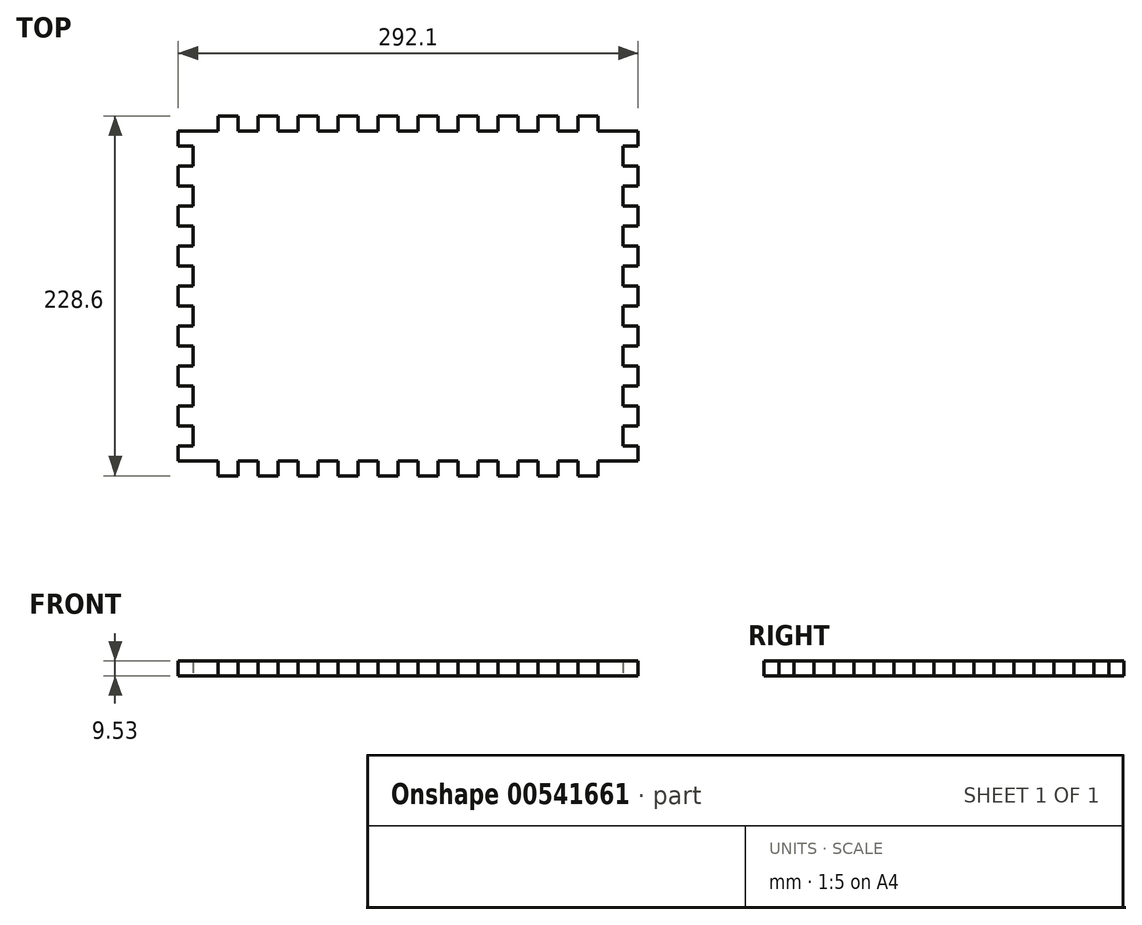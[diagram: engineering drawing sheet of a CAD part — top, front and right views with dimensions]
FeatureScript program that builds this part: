
annotation { "Feature Type Name" : "Feature", "Feature Type Description" : "" }
export const myFeature = defineFeature(function(context is Context, id is Id, definition is map)
    precondition{}
    {
        {
            var Q0;
            Q0=qCreatedBy(makeId("Top.planeOp"),FACE);
            var sketch = newSketch(context, id + "F0", { "sketchPlane" : qUnion([Q0])});
            skLineSegment(sketch, "E0.bottom", {"start": v(50.8, 0) * mm, "end": v(63.5, 0) * mm});
            skLineSegment(sketch, "E0.left", {"start": v(0, -9.53) * mm, "end": v(0, -19.05) * mm});
            skLineSegment(sketch, "E1", {"start": v(0, -9.53) * mm, "end": v(25.4, -9.53) * mm});
            skLineSegment(sketch, "E2", {"start": v(25.4, -9.53) * mm, "end": v(25.4, 0) * mm});
            skLineSegment(sketch, "E3", {"start": v(25.4, 0) * mm, "end": v(38.1, 0) * mm});
            skLineSegment(sketch, "E4", {"start": v(38.1, 0) * mm, "end": v(38.1, -9.53) * mm});
            skLineSegment(sketch, "E5", {"start": v(38.1, -9.53) * mm, "end": v(50.8, -9.53) * mm});
            skLineSegment(sketch, "E6", {"start": v(50.8, -9.53) * mm, "end": v(50.8, 0) * mm});
            skLineSegment(sketch, "E7", {"start": v(63.5, 0) * mm, "end": v(63.5, -9.52) * mm});
            skLineSegment(sketch, "E8", {"start": v(63.5, -9.52) * mm, "end": v(76.2, -9.52) * mm});
            skLineSegment(sketch, "E9", {"start": v(76.2, -9.52) * mm, "end": v(76.2, 0) * mm});
            skLineSegment(sketch, "E10", {"start": v(76.2, 0) * mm, "end": v(88.9, 0) * mm});
            skLineSegment(sketch, "E11", {"start": v(88.9, 0) * mm, "end": v(88.9, -9.52) * mm});
            skLineSegment(sketch, "E12", {"start": v(88.9, -9.52) * mm, "end": v(101.6, -9.52) * mm});
            skLineSegment(sketch, "E13", {"start": v(101.6, -9.52) * mm, "end": v(101.6, 0) * mm});
            skPoint(sketch, "E14.orphan", {"position": v(0, 0) * mm});
            skLineSegment(sketch, "E15.trimOffspring", {"start": v(101.6, 0) * mm, "end": v(114.3, 0) * mm});
            skLineSegment(sketch, "E16", {"start": v(114.3, 0) * mm, "end": v(114.3, -9.53) * mm});
            skLineSegment(sketch, "E17", {"start": v(114.3, -9.52) * mm, "end": v(127, -9.52) * mm});
            skLineSegment(sketch, "E18", {"start": v(127, -9.53) * mm, "end": v(127, 0) * mm});
            skLineSegment(sketch, "E19", {"start": v(127, 0) * mm, "end": v(139.7, 0) * mm});
            skLineSegment(sketch, "E20", {"start": v(139.7, 0) * mm, "end": v(139.7, -9.52) * mm});
            skLineSegment(sketch, "E21", {"start": v(139.7, -9.52) * mm, "end": v(152.4, -9.52) * mm});
            skLineSegment(sketch, "E22", {"start": v(152.4, -9.53) * mm, "end": v(152.4, 0) * mm});
            skLineSegment(sketch, "E23", {"start": v(152.4, 0) * mm, "end": v(165.1, 0) * mm});
            skLineSegment(sketch, "E24", {"start": v(165.1, 0) * mm, "end": v(165.1, -9.52) * mm});
            skLineSegment(sketch, "E25", {"start": v(165.1, -9.52) * mm, "end": v(177.8, -9.52) * mm});
            skLineSegment(sketch, "E26", {"start": v(177.8, -9.52) * mm, "end": v(177.8, 0) * mm});
            skLineSegment(sketch, "E27", {"start": v(177.8, 0) * mm, "end": v(190.5, 0) * mm});
            skLineSegment(sketch, "E28", {"start": v(190.5, 0) * mm, "end": v(190.5, -9.52) * mm});
            skLineSegment(sketch, "E29", {"start": v(190.5, -9.52) * mm, "end": v(203.2, -9.52) * mm});
            skLineSegment(sketch, "E30", {"start": v(203.2, -9.52) * mm, "end": v(203.2, 0) * mm});
            skLineSegment(sketch, "E31.trimOffspring", {"start": v(203.2, 0) * mm, "end": v(215.9, 0) * mm});
            skLineSegment(sketch, "E32", {"start": v(215.9, 0) * mm, "end": v(215.9, -9.52) * mm});
            skLineSegment(sketch, "E33", {"start": v(215.9, -9.52) * mm, "end": v(228.6, -9.52) * mm});
            skLineSegment(sketch, "E34", {"start": v(228.6, -9.52) * mm, "end": v(228.6, 0) * mm});
            skLineSegment(sketch, "E35.trimOffspring", {"start": v(228.6, 0) * mm, "end": v(241.3, 0) * mm});
            skLineSegment(sketch, "E36", {"start": v(241.3, 0) * mm, "end": v(241.3, -9.52) * mm});
            skLineSegment(sketch, "E37", {"start": v(241.3, -9.52) * mm, "end": v(254, -9.52) * mm});
            skLineSegment(sketch, "E38", {"start": v(254, -9.52) * mm, "end": v(254, 0) * mm});
            skLineSegment(sketch, "E39", {"start": v(254, 0) * mm, "end": v(266.7, 0) * mm});
            skLineSegment(sketch, "E40", {"start": v(266.7, 0) * mm, "end": v(266.7, -9.52) * mm});
            skLineSegment(sketch, "E41", {"start": v(266.7, -9.52) * mm, "end": v(292.1, -9.52) * mm});
            skPoint(sketch, "E42.orphan", {"position": v(292.1, 0) * mm});
            skLineSegment(sketch, "E43", {"start": v(0, -19.05) * mm, "end": v(9.52, -19.05) * mm});
            skLineSegment(sketch, "E44", {"start": v(9.52, -19.05) * mm, "end": v(9.52, -31.75) * mm});
            skLineSegment(sketch, "E45", {"start": v(9.52, -31.75) * mm, "end": v(0, -31.75) * mm});
            skLineSegment(sketch, "E46", {"start": v(0, -31.75) * mm, "end": v(0, -44.45) * mm});
            skLineSegment(sketch, "E47", {"start": v(0, -44.45) * mm, "end": v(9.52, -44.45) * mm});
            skLineSegment(sketch, "E48", {"start": v(9.52, -44.45) * mm, "end": v(9.52, -57.15) * mm});
            skLineSegment(sketch, "E49", {"start": v(9.52, -57.15) * mm, "end": v(0, -57.15) * mm});
            skLineSegment(sketch, "E50", {"start": v(0, -57.15) * mm, "end": v(0, -69.85) * mm});
            skLineSegment(sketch, "E51", {"start": v(0, -69.85) * mm, "end": v(9.52, -69.85) * mm});
            skLineSegment(sketch, "E52", {"start": v(9.52, -69.85) * mm, "end": v(9.52, -82.55) * mm});
            skLineSegment(sketch, "E53", {"start": v(9.52, -82.55) * mm, "end": v(0, -82.55) * mm});
            skLineSegment(sketch, "E54.trimOffspring", {"start": v(0, -82.55) * mm, "end": v(0, -95.25) * mm});
            skLineSegment(sketch, "E55", {"start": v(0, -95.25) * mm, "end": v(9.52, -95.25) * mm});
            skLineSegment(sketch, "E56", {"start": v(9.52, -95.25) * mm, "end": v(9.52, -107.95) * mm});
            skLineSegment(sketch, "E57", {"start": v(9.53, -107.95) * mm, "end": v(0, -107.95) * mm});
            skLineSegment(sketch, "E58", {"start": v(0, -107.95) * mm, "end": v(0, -120.65) * mm});
            skLineSegment(sketch, "E59", {"start": v(0, -120.65) * mm, "end": v(9.53, -120.65) * mm});
            skLineSegment(sketch, "E60", {"start": v(9.53, -120.65) * mm, "end": v(9.53, -133.35) * mm});
            skLineSegment(sketch, "E61", {"start": v(9.53, -133.35) * mm, "end": v(0, -133.35) * mm});
            skLineSegment(sketch, "E62", {"start": v(0, -133.35) * mm, "end": v(0, -146.05) * mm});
            skLineSegment(sketch, "E63", {"start": v(0, -146.05) * mm, "end": v(9.53, -146.05) * mm});
            skLineSegment(sketch, "E64", {"start": v(9.53, -146.05) * mm, "end": v(9.53, -158.75) * mm});
            skLineSegment(sketch, "E65", {"start": v(9.53, -158.75) * mm, "end": v(0, -158.75) * mm});
            skLineSegment(sketch, "E66.trimOffspring", {"start": v(0, -158.75) * mm, "end": v(0, -171.45) * mm});
            skLineSegment(sketch, "E67", {"start": v(0, -171.45) * mm, "end": v(9.53, -171.45) * mm});
            skLineSegment(sketch, "E68", {"start": v(9.53, -171.45) * mm, "end": v(9.53, -184.15) * mm});
            skLineSegment(sketch, "E69", {"start": v(9.53, -184.15) * mm, "end": v(0, -184.15) * mm});
            skLineSegment(sketch, "E70", {"start": v(0, -184.15) * mm, "end": v(0, -196.85) * mm});
            skLineSegment(sketch, "E71", {"start": v(0, -196.85) * mm, "end": v(9.53, -196.85) * mm});
            skLineSegment(sketch, "E72", {"start": v(9.53, -196.85) * mm, "end": v(9.53, -209.55) * mm});
            skLineSegment(sketch, "E73", {"start": v(9.53, -209.55) * mm, "end": v(0, -209.55) * mm});
            skLineSegment(sketch, "E74.trimOffspring", {"start": v(0, -209.55) * mm, "end": v(0, -219.07) * mm});
            skLineSegment(sketch, "E75", {"start": v(0, -219.07) * mm, "end": v(25.4, -219.07) * mm});
            skLineSegment(sketch, "E76", {"start": v(25.4, -219.08) * mm, "end": v(25.4, -228.6) * mm});
            skPoint(sketch, "E77.orphan", {"position": v(0, -228.6) * mm});
            skLineSegment(sketch, "E78", {"start": v(146.05, -9.52) * mm, "end": v(146.05, -60.11) * mm, "construction": true});
            skLineSegment(sketch, "E79", {"start": v(0, -114.3) * mm, "end": v(50, -114.3) * mm, "construction": true});
            skLineSegment(sketch, "E80.MirrorCS", {"start": v(292.1, -9.53) * mm, "end": v(292.1, -19.05) * mm});
            skLineSegment(sketch, "E81.MirrorCS", {"start": v(292.1, -19.05) * mm, "end": v(282.57, -19.05) * mm});
            skLineSegment(sketch, "E82.MirrorCS", {"start": v(282.57, -19.05) * mm, "end": v(282.57, -31.75) * mm});
            skLineSegment(sketch, "E83.MirrorCS", {"start": v(282.57, -31.75) * mm, "end": v(292.1, -31.75) * mm});
            skLineSegment(sketch, "E84.MirrorCS", {"start": v(292.1, -31.75) * mm, "end": v(292.1, -44.45) * mm});
            skLineSegment(sketch, "E85.MirrorCS", {"start": v(292.1, -44.45) * mm, "end": v(282.57, -44.45) * mm});
            skLineSegment(sketch, "E86.MirrorCS", {"start": v(282.57, -44.45) * mm, "end": v(282.57, -57.15) * mm});
            skLineSegment(sketch, "E87.MirrorCS", {"start": v(282.57, -57.15) * mm, "end": v(292.1, -57.15) * mm});
            skLineSegment(sketch, "E88.MirrorCS", {"start": v(292.1, -57.15) * mm, "end": v(292.1, -69.85) * mm});
            skLineSegment(sketch, "E89.MirrorCS", {"start": v(292.1, -69.85) * mm, "end": v(282.57, -69.85) * mm});
            skLineSegment(sketch, "E90.MirrorCS", {"start": v(282.57, -69.85) * mm, "end": v(282.57, -82.55) * mm});
            skLineSegment(sketch, "E91.MirrorCS", {"start": v(282.57, -82.55) * mm, "end": v(292.1, -82.55) * mm});
            skLineSegment(sketch, "E92.MirrorCS", {"start": v(292.1, -82.55) * mm, "end": v(292.1, -95.25) * mm});
            skLineSegment(sketch, "E93.MirrorCS", {"start": v(292.1, -95.25) * mm, "end": v(282.57, -95.25) * mm});
            skLineSegment(sketch, "E94.MirrorCS", {"start": v(282.57, -95.25) * mm, "end": v(282.57, -107.95) * mm});
            skLineSegment(sketch, "E95.MirrorCS", {"start": v(282.57, -107.95) * mm, "end": v(292.1, -107.95) * mm});
            skLineSegment(sketch, "E96.MirrorCS", {"start": v(292.1, -107.95) * mm, "end": v(292.1, -120.65) * mm});
            skLineSegment(sketch, "E97.MirrorCS", {"start": v(292.1, -120.65) * mm, "end": v(282.57, -120.65) * mm});
            skLineSegment(sketch, "E98.MirrorCS", {"start": v(282.57, -133.35) * mm, "end": v(292.1, -133.35) * mm});
            skLineSegment(sketch, "E99.MirrorCS", {"start": v(292.1, -133.35) * mm, "end": v(292.1, -146.05) * mm});
            skLineSegment(sketch, "E100.MirrorCS", {"start": v(292.1, -146.05) * mm, "end": v(282.57, -146.05) * mm});
            skLineSegment(sketch, "E101.MirrorCS", {"start": v(282.57, -146.05) * mm, "end": v(282.57, -158.75) * mm});
            skLineSegment(sketch, "E102.MirrorCS", {"start": v(282.57, -158.75) * mm, "end": v(292.1, -158.75) * mm});
            skLineSegment(sketch, "E103.MirrorCS", {"start": v(292.1, -158.75) * mm, "end": v(292.1, -171.45) * mm});
            skLineSegment(sketch, "E104.MirrorCS", {"start": v(292.1, -171.45) * mm, "end": v(282.57, -171.45) * mm});
            skLineSegment(sketch, "E105.MirrorCS", {"start": v(282.57, -171.45) * mm, "end": v(282.57, -184.15) * mm});
            skLineSegment(sketch, "E106.MirrorCS", {"start": v(282.57, -184.15) * mm, "end": v(292.1, -184.15) * mm});
            skLineSegment(sketch, "E107.MirrorCS", {"start": v(292.1, -184.15) * mm, "end": v(292.1, -196.85) * mm});
            skLineSegment(sketch, "E108.MirrorCS", {"start": v(292.1, -196.85) * mm, "end": v(282.57, -196.85) * mm});
            skLineSegment(sketch, "E109.MirrorCS", {"start": v(282.57, -196.85) * mm, "end": v(282.57, -209.55) * mm});
            skLineSegment(sketch, "E110.MirrorCS", {"start": v(282.57, -209.55) * mm, "end": v(292.1, -209.55) * mm});
            skLineSegment(sketch, "E111.MirrorCS", {"start": v(292.1, -209.55) * mm, "end": v(292.1, -219.07) * mm});
            skLineSegment(sketch, "E112.MirrorCS", {"start": v(292.1, -219.07) * mm, "end": v(266.7, -219.07) * mm});
            skLineSegment(sketch, "E113.MirrorCS", {"start": v(266.7, -219.08) * mm, "end": v(266.7, -228.6) * mm});
            skLineSegment(sketch, "E114.MirrorCS", {"start": v(25.4, -228.6) * mm, "end": v(38.1, -228.6) * mm});
            skLineSegment(sketch, "E115.MirrorCS", {"start": v(38.1, -228.6) * mm, "end": v(38.1, -219.08) * mm});
            skLineSegment(sketch, "E116.MirrorCS", {"start": v(38.1, -219.08) * mm, "end": v(50.8, -219.08) * mm});
            skLineSegment(sketch, "E117.MirrorCS", {"start": v(50.8, -219.08) * mm, "end": v(50.8, -228.6) * mm});
            skLineSegment(sketch, "E118.MirrorCS", {"start": v(50.8, -228.6) * mm, "end": v(63.5, -228.6) * mm});
            skLineSegment(sketch, "E119.MirrorCS", {"start": v(63.5, -228.6) * mm, "end": v(63.5, -219.08) * mm});
            skLineSegment(sketch, "E120.MirrorCS", {"start": v(63.5, -219.08) * mm, "end": v(76.2, -219.08) * mm});
            skLineSegment(sketch, "E121.MirrorCS", {"start": v(76.2, -219.08) * mm, "end": v(76.2, -228.6) * mm});
            skLineSegment(sketch, "E122.MirrorCS", {"start": v(76.2, -228.6) * mm, "end": v(88.9, -228.6) * mm});
            skLineSegment(sketch, "E123.MirrorCS", {"start": v(88.9, -228.6) * mm, "end": v(88.9, -219.08) * mm});
            skLineSegment(sketch, "E124.MirrorCS", {"start": v(88.9, -219.08) * mm, "end": v(101.6, -219.08) * mm});
            skLineSegment(sketch, "E125.MirrorCS", {"start": v(101.6, -219.08) * mm, "end": v(101.6, -228.6) * mm});
            skLineSegment(sketch, "E126.MirrorCS", {"start": v(101.6, -228.6) * mm, "end": v(114.3, -228.6) * mm});
            skLineSegment(sketch, "E127.MirrorCS", {"start": v(114.3, -228.6) * mm, "end": v(114.3, -219.08) * mm});
            skLineSegment(sketch, "E128.MirrorCS", {"start": v(114.3, -219.08) * mm, "end": v(127, -219.08) * mm});
            skLineSegment(sketch, "E129.MirrorCS", {"start": v(127, -219.08) * mm, "end": v(127, -228.6) * mm});
            skLineSegment(sketch, "E130.MirrorCS", {"start": v(127, -228.6) * mm, "end": v(139.7, -228.6) * mm});
            skLineSegment(sketch, "E131.MirrorCS", {"start": v(139.7, -228.6) * mm, "end": v(139.7, -219.08) * mm});
            skLineSegment(sketch, "E132.MirrorCS", {"start": v(139.7, -219.08) * mm, "end": v(152.4, -219.08) * mm});
            skLineSegment(sketch, "E133.MirrorCS", {"start": v(152.4, -219.08) * mm, "end": v(152.4, -228.6) * mm});
            skLineSegment(sketch, "E134.MirrorCS", {"start": v(152.4, -228.6) * mm, "end": v(165.1, -228.6) * mm});
            skLineSegment(sketch, "E135.MirrorCS", {"start": v(165.1, -228.6) * mm, "end": v(165.1, -219.08) * mm});
            skLineSegment(sketch, "E136.MirrorCS", {"start": v(165.1, -219.08) * mm, "end": v(177.8, -219.08) * mm});
            skLineSegment(sketch, "E137.MirrorCS", {"start": v(177.8, -219.08) * mm, "end": v(177.8, -228.6) * mm});
            skLineSegment(sketch, "E138.MirrorCS", {"start": v(177.8, -228.6) * mm, "end": v(190.5, -228.6) * mm});
            skLineSegment(sketch, "E139.MirrorCS", {"start": v(190.5, -228.6) * mm, "end": v(190.5, -219.08) * mm});
            skLineSegment(sketch, "E140.MirrorCS", {"start": v(190.5, -219.08) * mm, "end": v(203.2, -219.08) * mm});
            skLineSegment(sketch, "E141.MirrorCS", {"start": v(203.2, -219.08) * mm, "end": v(203.2, -228.6) * mm});
            skLineSegment(sketch, "E142.MirrorCS", {"start": v(203.2, -228.6) * mm, "end": v(215.9, -228.6) * mm});
            skLineSegment(sketch, "E143.MirrorCS", {"start": v(215.9, -228.6) * mm, "end": v(215.9, -219.08) * mm});
            skLineSegment(sketch, "E144.MirrorCS", {"start": v(215.9, -219.08) * mm, "end": v(228.6, -219.08) * mm});
            skLineSegment(sketch, "E145.MirrorCS", {"start": v(228.6, -219.08) * mm, "end": v(228.6, -228.6) * mm});
            skLineSegment(sketch, "E146.MirrorCS", {"start": v(228.6, -228.6) * mm, "end": v(241.3, -228.6) * mm});
            skLineSegment(sketch, "E147.MirrorCS", {"start": v(241.3, -228.6) * mm, "end": v(241.3, -219.08) * mm});
            skLineSegment(sketch, "E148.MirrorCS", {"start": v(241.3, -219.08) * mm, "end": v(254, -219.08) * mm});
            skLineSegment(sketch, "E149.MirrorCS", {"start": v(254, -219.08) * mm, "end": v(254, -228.6) * mm});
            skLineSegment(sketch, "E150.MirrorCS", {"start": v(254, -228.6) * mm, "end": v(266.7, -228.6) * mm});
            skLineSegment(sketch, "E151.MirrorCS", {"start": v(266.7, -228.6) * mm, "end": v(266.7, -219.08) * mm});
            skLineSegment(sketch, "E152.MirrorCS", {"start": v(266.7, -219.08) * mm, "end": v(292.1, -219.08) * mm});
            skLineSegment(sketch, "E153", {"start": v(282.57, -120.65) * mm, "end": v(282.57, -133.35) * mm});
            skSolve(sketch);
        }
        {
            var Q0;
            Q0=makeQuery(id+"F0.imprint","IMPRINT",FACE,{"disambiguationData":[TD([[makeQuery(id+"F0.imprint","IMPRINT",EDGE,{"derivedFrom":sQuery(id+"F0.wireOp",EDGE,"E1")}),-1.0]])]});
            extrude(context, id + "F1", {"entities" : qUnion([Q0]), "depth" : 9.52 * mm, "offsetDistance" : 25.4 * mm});
        }
    });
